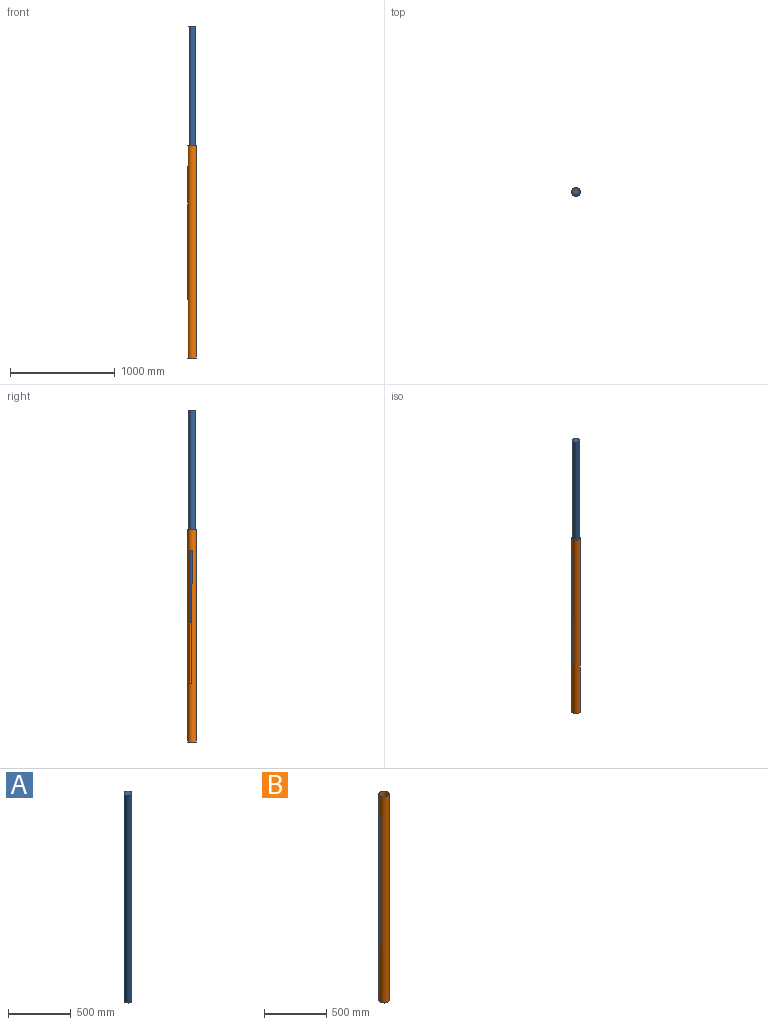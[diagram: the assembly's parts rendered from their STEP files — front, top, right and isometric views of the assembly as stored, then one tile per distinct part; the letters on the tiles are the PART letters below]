
ASSEMBLY  parts=2 mates=1
PART A: 3 faces, bbox 63.5x63.5x2032 mm
  f0: cylinder r=31.75mm len=2032mm, axis (0,0,-1), area 405366mm2, adj f1,f2
  f1: plane 63.5x63.5mm, normal (0,0,1), area 3166.9mm2, adj f0
  f2: plane 63.5x63.5mm, normal (0,0,-1), area 3166.9mm2, adj f0
PART B: 8 faces, bbox 82.6x82.6x2032 mm
  f0: cylinder r=38.1mm len=2032mm, axis (0,0,-1), area 451129.8mm2, adj f2,f3,f4,f5,f6,f7
  f1: cylinder r=41.27mm len=2032mm, axis (0,0,-1), area 492228.4mm2, adj f2,f3,f4,f5,f6,f7
  f2: plane 82.55x82.55mm, normal (0,0,1), area 791.7mm2, adj f0,f1
  f3: plane 82.55x82.55mm, normal (0,0,-1), area 791.7mm2, adj f0,f1
  f4: plane 1270x4.14mm, normal (0,-1,0), area 5252.7mm2, adj f0,f1,f5,f7
  f5: plane 25.4x12.88mm, normal (0,0,-1), area 87.5mm2, adj f0,f1,f4,f6
  f6: plane 1270x3.18mm, normal (0,1,0), area 4032.2mm2, adj f0,f1,f5,f7
  f7: plane 25.4x12.88mm, normal (0,0,1), area 87.5mm2, adj f0,f1,f4,f6
PLACE A t=(1747.77,-214.89,229.49)mm
PLACE B t=(1747.77,-214.89,-912.9)mm
MATE cylindrical B.f0 <-> A.f0  axis (0,0,-1) through (1747.77,-214.89,1119.1)mm
